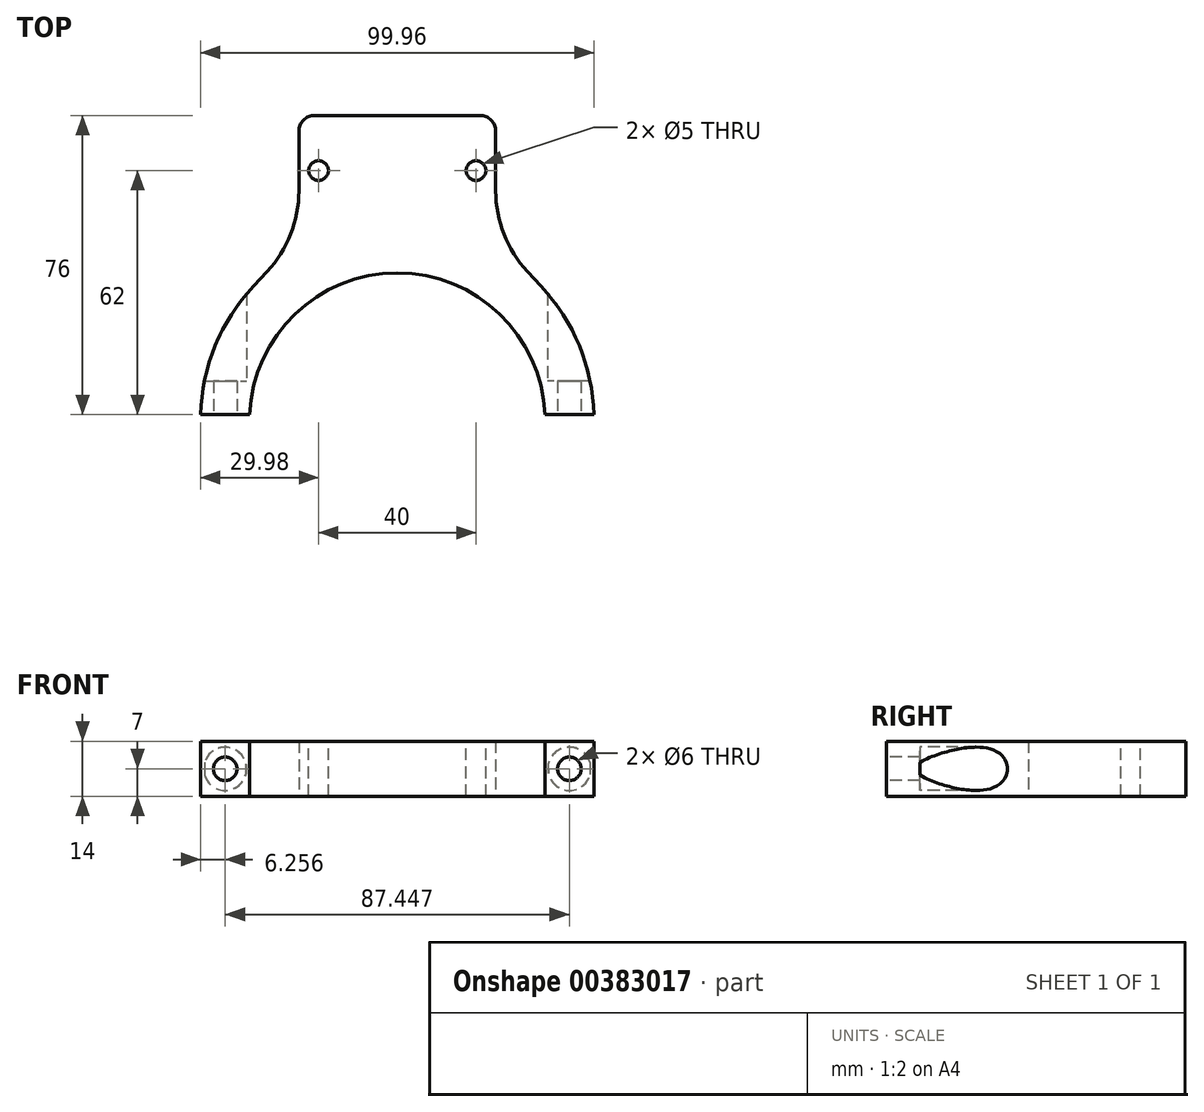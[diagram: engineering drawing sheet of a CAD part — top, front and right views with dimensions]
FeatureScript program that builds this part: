
annotation { "Feature Type Name" : "Feature", "Feature Type Description" : "" }
export const myFeature = defineFeature(function(context is Context, id is Id, definition is map)
    precondition{}
    {
        {
            var Q0;
            Q0=qCreatedBy(makeId("Top.planeOp"),FACE);
            var sketch = newSketch(context, id + "F0", { "sketchPlane" : qUnion([Q0])});
            skCircle(sketch, "E0", {"center": v(0, 0) * mm, "radius": 37.5 * mm});
            skCircle(sketch, "E1", {"center": v(0, 0) * mm, "radius": 50 * mm});
            skSolve(sketch);
        }
        {
            var Q0;
            Q0 = qSketchRegion(id + "F0", true);
            extrude(context, id + "F1", {"entities" : qUnion([Q0]), "depth" : 14 * mm, "offsetDistance" : 25 * mm});
        }
        {
            var Q0;
            Q0=makeQuery(id+"F1.opExtrude","CAP_FACE",FACE,{"disambiguationData":[OSD([sQuery(id+"F0.wireOp",EDGE,"E0"),sQuery(id+"F0.wireOp",EDGE,"E1")])],"isStart":false});
            var sketch = newSketch(context, id + "F2", { "sketchPlane" : qUnion([Q0])});
            skLineSegment(sketch, "E2.bottom", {"start": v(-55, 1.5) * mm, "end": v(55, 1.5) * mm});
            skLineSegment(sketch, "E2.top", {"start": v(-55, -63.4) * mm, "end": v(55, -63.4) * mm});
            skLineSegment(sketch, "E2.left", {"start": v(-55, 1.5) * mm, "end": v(-55, -63.4) * mm});
            skLineSegment(sketch, "E2.right", {"start": v(55, 1.5) * mm, "end": v(55, -63.4) * mm});
            skSolve(sketch);
        }
        {
            var Q0;
            Q0 = qSketchRegion(id + "F2", true);
            extrude(context, id + "F3", {"entities" : qUnion([Q0]), "operationType" : NewBodyOperationType.REMOVE, "endBound" : BoundingType.THROUGH_ALL, "oppositeDirection" : true, "depth" : 25 * mm, "offsetDistance" : 25 * mm});
        }
        {
            var Q0;
            Q0=qCreatedBy(makeId("Front.planeOp"),FACE);
            var sketch = newSketch(context, id + "F4", { "sketchPlane" : qUnion([Q0])});
            skLineSegment(sketch, "E3.0.0", {"start": v(-37.47, 14) * mm, "end": v(-49.98, 14) * mm, "construction": true});
            skLineSegment(sketch, "E3.0.1", {"start": v(-49.98, 14) * mm, "end": v(-49.98, 0) * mm, "construction": true});
            skLineSegment(sketch, "E3.0.2", {"start": v(-49.98, 0) * mm, "end": v(-37.47, 0) * mm, "construction": true});
            skLineSegment(sketch, "E3.0.3", {"start": v(-37.47, 0) * mm, "end": v(-37.47, 14) * mm, "construction": true});
            skLineSegment(sketch, "E4.0.0", {"start": v(37.47, 0) * mm, "end": v(49.98, 0) * mm, "construction": true});
            skLineSegment(sketch, "E4.0.1", {"start": v(49.98, 0) * mm, "end": v(49.98, 14) * mm, "construction": true});
            skLineSegment(sketch, "E4.0.2", {"start": v(49.98, 14) * mm, "end": v(37.47, 14) * mm, "construction": true});
            skLineSegment(sketch, "E4.0.3", {"start": v(37.47, 0) * mm, "end": v(37.47, 14) * mm, "construction": true});
            skLineSegment(sketch, "E5", {"start": v(-49.98, 14) * mm, "end": v(-37.47, 0) * mm, "construction": true});
            skLineSegment(sketch, "E6", {"start": v(-37.47, 14) * mm, "end": v(-49.98, 0) * mm, "construction": true});
            skLineSegment(sketch, "E7", {"start": v(37.47, 14) * mm, "end": v(49.98, 0) * mm, "construction": true});
            skLineSegment(sketch, "E8", {"start": v(49.98, 14) * mm, "end": v(37.47, 0) * mm, "construction": true});
            skCircle(sketch, "E9", {"center": v(-43.72, 7) * mm, "radius": 3 * mm});
            skCircle(sketch, "E10", {"center": v(43.72, 7) * mm, "radius": 3 * mm});
            skSolve(sketch);
        }
        {
            var Q0;
            Q0 = qSketchRegion(id + "F4", true);
            extrude(context, id + "F5", {"entities" : qUnion([Q0]), "operationType" : NewBodyOperationType.REMOVE, "endBound" : BoundingType.THROUGH_ALL, "oppositeDirection" : true, "depth" : 25 * mm, "offsetDistance" : 25 * mm});
        }
        {
            var Q0;
            Q0=qCreatedBy(makeId("Front.planeOp"),FACE);
            cPlane(context, id + "F6", {"entities" : qUnion([Q0]), "cplaneType" : CPlaneType.OFFSET, "offset" : 10 * mm, "oppositeDirection" : true, "width" : 150 * mm, "height" : 150 * mm});
        }
        {
            var Q0;
            Q0=qCreatedBy(id+"F6.planeOp",FACE);
            var sketch = newSketch(context, id + "F7", { "sketchPlane" : qUnion([Q0])});
            skCircle(sketch, "E11.0", {"center": v(43.72, 7) * mm, "radius": 3 * mm, "construction": true});
            skCircle(sketch, "E12.0", {"center": v(-43.72, 7) * mm, "radius": 3 * mm, "construction": true});
            skCircle(sketch, "E13", {"center": v(43.72, 7) * mm, "radius": 5.5 * mm});
            skCircle(sketch, "E14", {"center": v(-43.72, 7) * mm, "radius": 5.5 * mm});
            skSolve(sketch);
        }
        {
            var Q0;
            Q0 = qSketchRegion(id + "F7", true);
            extrude(context, id + "F8", {"entities" : qUnion([Q0]), "operationType" : NewBodyOperationType.REMOVE, "oppositeDirection" : true, "depth" : 25 * mm, "offsetDistance" : 25 * mm});
        }
        {
            var Q0;
            Q0=qCreatedBy(makeId("Top.planeOp"),FACE);
            var sketch = newSketch(context, id + "F9", { "sketchPlane" : qUnion([Q0])});
            skLineSegment(sketch, "E15", {"start": v(29.62, 46.5) * mm, "end": v(-52.53, 46.5) * mm, "construction": true});
            skLineSegment(sketch, "E16", {"start": v(21, 77.5) * mm, "end": v(-21, 77.5) * mm, "construction": true});
            skLineSegment(sketch, "E17", {"start": v(0, 0) * mm, "end": v(0, 104) * mm, "construction": true});
            skLineSegment(sketch, "E18.bottom", {"start": v(25, 77.5) * mm, "end": v(-25, 77.5) * mm});
            skLineSegment(sketch, "E18.top", {"start": v(25, 46.5) * mm, "end": v(-25, 46.5) * mm});
            skLineSegment(sketch, "E18.left", {"start": v(25, 73.5) * mm, "end": v(25, 58.32) * mm});
            skLineSegment(sketch, "E18.right", {"start": v(-25, 73.5) * mm, "end": v(-25, 58.32) * mm});
            skLineSegment(sketch, "E19.0.0", {"start": v(-37.47, 1.5) * mm, "end": v(-49.98, 1.5) * mm, "construction": true});
            skArc(sketch, "E19.0.1", {"start": v(-49.98, 1.5) * mm, "mid": v(0, 50) * mm, "end": v(49.98, 1.5) * mm, "construction": true});
            skLineSegment(sketch, "E19.0.2", {"start": v(49.98, 1.5) * mm, "end": v(37.47, 1.5) * mm, "construction": true});
            skArc(sketch, "E19.0.3", {"start": v(37.47, 1.5) * mm, "mid": v(0, 37.5) * mm, "end": v(-37.47, 1.5) * mm, "construction": true});
            skLineSegment(sketch, "E20", {"start": v(33.06, 37.86) * mm, "end": v(36.56, 34.1) * mm});
            skLineSegment(sketch, "E21", {"start": v(-33.06, 37.86) * mm, "end": v(-36.56, 34.1) * mm});
            skPoint(sketch, "E22.visualSharp", {"position": v(25, 46.5) * mm});
            skArc(sketch, "E22.filletArc", {"start": v(25, 58.32) * mm, "mid": v(27.09, 47.32) * mm, "end": v(33.06, 37.86) * mm});
            skPoint(sketch, "E23.visualSharp", {"position": v(-25, 46.5) * mm});
            skArc(sketch, "E23.filletArc", {"start": v(-33.06, 37.86) * mm, "mid": v(-27.09, 47.32) * mm, "end": v(-25, 58.32) * mm});
            skArc(sketch, "E24.filletArc", {"start": v(25, 73.5) * mm, "mid": v(23.83, 76.33) * mm, "end": v(21, 77.5) * mm});
            skArc(sketch, "E25.filletArc", {"start": v(-21, 77.5) * mm, "mid": v(-23.83, 76.33) * mm, "end": v(-25, 73.5) * mm});
            skLineSegment(sketch, "E26", {"start": v(36.56, 34.1) * mm, "end": v(0, 41.86) * mm});
            skLineSegment(sketch, "E27", {"start": v(0, 41.86) * mm, "end": v(-36.56, 34.1) * mm});
            skSolve(sketch);
        }
        {
            var Q0;
            Q0 = qSketchRegion(id + "F9", true);
            var Q1;
            Q1=makeQuery(id+"F1.opExtrude","CAP_FACE",FACE,{"disambiguationData":[OSD([sQuery(id+"F0.wireOp",EDGE,"E0"),sQuery(id+"F0.wireOp",EDGE,"E1")])],"isStart":false});
            extrude(context, id + "F10", {"entities" : qUnion([Q0]), "operationType" : NewBodyOperationType.ADD, "endBound" : BoundingType.UP_TO_SURFACE, "depth" : 25 * mm, "endBoundEntityFace" : qUnion([Q1]), "offsetDistance" : 25 * mm});
        }
        {
            var Q0;
            Q0=makeQuery(id+"F10.boolean.opBoolean","MERGE",FACE,{"derivedFrom":[makeQuery(id+"F1.opExtrude","CAP_FACE",FACE,{"disambiguationData":[OSD([sQuery(id+"F0.wireOp",EDGE,"E0"),sQuery(id+"F0.wireOp",EDGE,"E1")])],"isStart":false}),makeQuery(id+"F10.opExtrude","CAP_FACE",FACE,{"disambiguationData":[OSD([sQuery(id+"F9.wireOp",EDGE,"E18.bottom"),sQuery(id+"F9.wireOp",EDGE,"E18.left"),sQuery(id+"F9.wireOp",EDGE,"E18.right"),sQuery(id+"F9.wireOp",EDGE,"E20"),sQuery(id+"F9.wireOp",EDGE,"E21"),sQuery(id+"F9.wireOp",EDGE,"E22.filletArc"),sQuery(id+"F9.wireOp",EDGE,"E23.filletArc"),sQuery(id+"F9.wireOp",EDGE,"E24.filletArc"),sQuery(id+"F9.wireOp",EDGE,"E25.filletArc"),sQuery(id+"F9.wireOp",EDGE,"E26"),sQuery(id+"F9.wireOp",EDGE,"E27")])],"isStart":false})]});
            var sketch = newSketch(context, id + "F11", { "sketchPlane" : qUnion([Q0])});
            skLineSegment(sketch, "E28", {"start": v(-40.48, 49.5) * mm, "end": v(55.27, 49.5) * mm, "construction": true});
            skLineSegment(sketch, "E29.0", {"start": v(21, 77.5) * mm, "end": v(-21, 77.5) * mm, "construction": true});
            skLineSegment(sketch, "E30", {"start": v(-38.33, 63.5) * mm, "end": v(72.16, 63.5) * mm, "construction": true});
            skCircle(sketch, "E31", {"center": v(-20, 63.5) * mm, "radius": 2.5 * mm});
            skCircle(sketch, "E32", {"center": v(20, 63.5) * mm, "radius": 2.5 * mm});
            skSolve(sketch);
        }
        {
            var Q0;
            Q0 = qSketchRegion(id + "F11", true);
            extrude(context, id + "F12", {"entities" : qUnion([Q0]), "operationType" : NewBodyOperationType.REMOVE, "endBound" : BoundingType.THROUGH_ALL, "oppositeDirection" : true, "depth" : 25 * mm, "offsetDistance" : 25 * mm});
        }
    });
